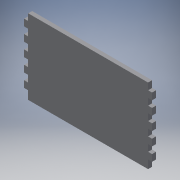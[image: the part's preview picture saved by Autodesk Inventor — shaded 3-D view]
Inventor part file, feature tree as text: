
AUTODESK INVENTOR PART (.ipt)
format: ipt  version: 2019 (Build 230136000, 136)  size: 137,216 bytes
history: native  units: mm
features: reference x15, other x6, extrude x1, sketch x1
ambient origin geometry x8: Origin, YZ Plane, XZ Plane, XY Plane, X Axis, Y Axis, Z Axis, Center Point
bodies: Body1 (feature_tree)
feature tree (23):
  other  "Твердое тело1"
  other  "РабПлоскость1"
  extrude  "Выдавливание1"  Depth=6.0mm TaperAngle=0.0deg
  sketch  "Эскиз1"
  reference  "Ссылка1"
  reference  "Ссылка2"
  reference  "Ссылка3"
  reference  "Ссылка4"
  reference  "Ссылка5"
  reference  "Ссылка6"
  reference  "Ссылка7"
  reference  "Ссылка8"
  reference  "Ссылка9"
  reference  "Ссылка10"
  reference  "Ссылка11"
  reference  "Ссылка12"
  reference  "Ссылка13"
  reference  "Ссылка14"
  reference  "Ссылка15"
  other  "<userpath>\Desktop\Новая папка (7)\Сборка2.iam"
  other  "Сборка2.iam"
  other  "боковина:1"
  other  "боковина:2"
